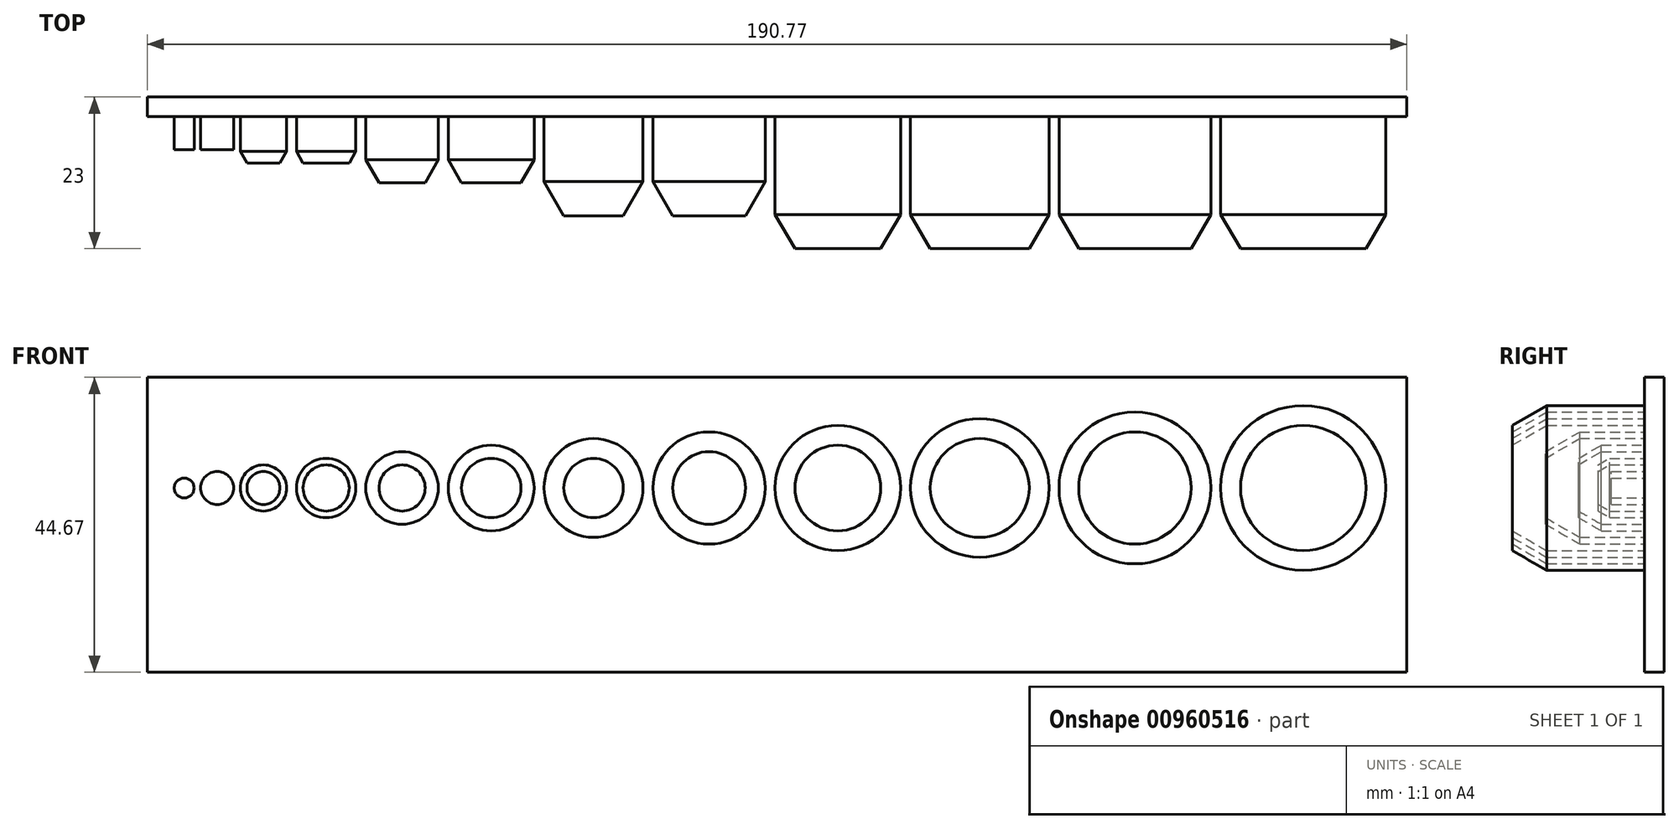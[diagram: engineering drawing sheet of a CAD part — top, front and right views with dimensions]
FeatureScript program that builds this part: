
annotation { "Feature Type Name" : "Feature", "Feature Type Description" : "" }
export const myFeature = defineFeature(function(context is Context, id is Id, definition is map)
    precondition{}
    {
        {
            var Q0;
            Q0=qCreatedBy(makeId("Front.planeOp"),FACE);
            var sketch = newSketch(context, id + "F0", { "sketchPlane" : qUnion([Q0])});
            skLineSegment(sketch, "E0", {"start": v(-30.94, 0) * mm, "end": v(30.94, 0) * mm, "construction": true});
            skCircle(sketch, "E1", {"center": v(-19.6, 0) * mm, "radius": 1.5 * mm});
            skCircle(sketch, "E2", {"center": v(-14.6, 0) * mm, "radius": 2.5 * mm});
            skCircle(sketch, "E3", {"center": v(-19.6, 0) * mm, "radius": 1.59 * mm});
            skCircle(sketch, "E4", {"center": v(-7.6, 0) * mm, "radius": 3.5 * mm});
            skCircle(sketch, "E5", {"center": v(1.9, 0) * mm, "radius": 4.5 * mm});
            skCircle(sketch, "E6", {"center": v(13.4, 0) * mm, "radius": 5.5 * mm});
            skCircle(sketch, "E7", {"center": v(26.9, 0) * mm, "radius": 6.5 * mm});
            skCircle(sketch, "E8", {"center": v(42.4, 0) * mm, "radius": 7.5 * mm});
            skCircle(sketch, "E9", {"center": v(59.9, 0) * mm, "radius": 8.5 * mm});
            skCircle(sketch, "E10", {"center": v(79.4, 0) * mm, "radius": 9.5 * mm});
            skLineSegment(sketch, "E11", {"start": v(50.7, 0) * mm, "end": v(122.59, 0) * mm, "construction": true});
            skCircle(sketch, "E12", {"center": v(100.9, 0) * mm, "radius": 10.5 * mm});
            skLineSegment(sketch, "E13", {"start": v(119.58, 0) * mm, "end": v(157.4, 0) * mm, "construction": true});
            skCircle(sketch, "E14", {"center": v(124.4, 0) * mm, "radius": 11.5 * mm});
            skCircle(sketch, "E15", {"center": v(149.9, 0) * mm, "radius": 12.5 * mm});
            skText(sketch, "E16", { "text": "25", "fontName": "OpenSans-Bold.ttf"});
            const initialGuessF0  = {"E16": [0.14266, -0.02711, 1, 0, 0.0101]};
            skSetInitialGuess(sketch, initialGuessF0);
            skSolve(sketch);
        }
        {
            var Q0;
            Q0=makeQuery(id+"F0.imprint","IMPRINT",FACE,{"disambiguationData":[TD([[makeQuery(id+"F0.imprint","IMPRINT",EDGE,{"derivedFrom":sQuery(id+"F0.wireOp",EDGE,"E1")}),1.0]])]});
            var Q1;
            Q1=makeQuery(id+"F0.imprint","IMPRINT",FACE,{"disambiguationData":[TD([[makeQuery(id+"F0.imprint","IMPRINT",EDGE,{"derivedFrom":sQuery(id+"F0.wireOp",EDGE,"E2")}),1.0]])]});
            extrude(context, id + "F1", {"entities" : qUnion([Q0, Q1]), "depth" : 5 * mm, "offsetDistance" : 25 * mm});
        }
        {
            var Q0;
            Q0=makeQuery(id+"F0.imprint","IMPRINT",FACE,{"disambiguationData":[TD([[makeQuery(id+"F0.imprint","IMPRINT",EDGE,{"derivedFrom":sQuery(id+"F0.wireOp",EDGE,"E4")}),1.0]])]});
            var Q1;
            Q1=makeQuery(id+"F0.imprint","IMPRINT",FACE,{"disambiguationData":[TD([[makeQuery(id+"F0.imprint","IMPRINT",EDGE,{"derivedFrom":sQuery(id+"F0.wireOp",EDGE,"E5")}),1.0]])]});
            extrude(context, id + "F2", {"entities" : qUnion([Q0, Q1]), "depth" : 7 * mm, "offsetDistance" : 25 * mm});
        }
        {
            var Q0;
            Q0=makeQuery(id+"F0.imprint","IMPRINT",FACE,{"disambiguationData":[TD([[makeQuery(id+"F0.imprint","IMPRINT",EDGE,{"derivedFrom":sQuery(id+"F0.wireOp",EDGE,"E6")}),1.0]])]});
            var Q1;
            Q1=makeQuery(id+"F0.imprint","IMPRINT",FACE,{"disambiguationData":[TD([[makeQuery(id+"F0.imprint","IMPRINT",EDGE,{"derivedFrom":sQuery(id+"F0.wireOp",EDGE,"E7")}),1.0]])]});
            extrude(context, id + "F3", {"entities" : qUnion([Q0, Q1]), "depth" : 10 * mm, "offsetDistance" : 25 * mm});
        }
        {
            var Q0;
            Q0=makeQuery(id+"F0.imprint","IMPRINT",FACE,{"disambiguationData":[TD([[makeQuery(id+"F0.imprint","IMPRINT",EDGE,{"derivedFrom":sQuery(id+"F0.wireOp",EDGE,"E8")}),1.0]])]});
            var Q1;
            Q1=makeQuery(id+"F0.imprint","IMPRINT",FACE,{"disambiguationData":[TD([[makeQuery(id+"F0.imprint","IMPRINT",EDGE,{"derivedFrom":sQuery(id+"F0.wireOp",EDGE,"E9")}),1.0]])]});
            extrude(context, id + "F4", {"entities" : qUnion([Q0, Q1]), "depth" : 15 * mm, "offsetDistance" : 25 * mm});
        }
        {
            var Q0;
            Q0=makeQuery(id+"F0.imprint","IMPRINT",FACE,{"disambiguationData":[TD([[makeQuery(id+"F0.imprint","IMPRINT",EDGE,{"derivedFrom":sQuery(id+"F0.wireOp",EDGE,"E10")}),1.0]])]});
            var Q1;
            Q1=makeQuery(id+"F0.imprint","IMPRINT",FACE,{"disambiguationData":[TD([[makeQuery(id+"F0.imprint","IMPRINT",EDGE,{"derivedFrom":sQuery(id+"F0.wireOp",EDGE,"E12")}),1.0]])]});
            extrude(context, id + "F5", {"entities" : qUnion([Q0, Q1]), "depth" : 20 * mm, "offsetDistance" : 25 * mm});
        }
        {
            var Q0;
            Q0=makeQuery(id+"F0.imprint","IMPRINT",FACE,{"disambiguationData":[TD([[makeQuery(id+"F0.imprint","IMPRINT",EDGE,{"derivedFrom":sQuery(id+"F0.wireOp",EDGE,"E14")}),1.0]])]});
            var Q1;
            Q1=makeQuery(id+"F0.imprint","IMPRINT",FACE,{"disambiguationData":[TD([[makeQuery(id+"F0.imprint","IMPRINT",EDGE,{"derivedFrom":sQuery(id+"F0.wireOp",EDGE,"E15")}),1.0]])]});
            extrude(context, id + "F6", {"entities" : qUnion([Q0, Q1]), "depth" : 20 * mm, "offsetDistance" : 25 * mm});
        }
        {
            var Q0;
            Q0=qCreatedBy(makeId("Front.planeOp"),FACE);
            var sketch = newSketch(context, id + "F7", { "sketchPlane" : qUnion([Q0])});
            skLineSegment(sketch, "E17.bottom", {"start": v(165.58, 16.76) * mm, "end": v(-25.2, 16.76) * mm});
            skLineSegment(sketch, "E17.top", {"start": v(165.58, -27.91) * mm, "end": v(-25.2, -27.91) * mm});
            skLineSegment(sketch, "E17.left", {"start": v(165.58, 16.76) * mm, "end": v(165.58, -27.91) * mm});
            skLineSegment(sketch, "E17.right", {"start": v(-25.2, 16.76) * mm, "end": v(-25.2, -27.91) * mm});
            skSolve(sketch);
        }
        {
            var Q0;
            Q0 = qSketchRegion(id + "F7", true);
            extrude(context, id + "F8", {"entities" : qUnion([Q0]), "oppositeDirection" : true, "depth" : 3 * mm, "offsetDistance" : 25 * mm});
        }
        {
            var Q0;
            Q0=makeQuery(id+"F6.opExtrude","CAP_EDGE",EDGE,{"disambiguationData":[OSD([sQuery(id+"F0.wireOp",EDGE,"E15")])],"isStart":false});
            var Q1;
            Q1=makeQuery(id+"F6.opExtrude","CAP_EDGE",EDGE,{"disambiguationData":[OSD([sQuery(id+"F0.wireOp",EDGE,"E14")])],"isStart":false});
            var Q2;
            Q2=makeQuery(id+"F5.opExtrude","CAP_EDGE",EDGE,{"disambiguationData":[OSD([sQuery(id+"F0.wireOp",EDGE,"E12")])],"isStart":false});
            var Q3;
            Q3=makeQuery(id+"F5.opExtrude","CAP_EDGE",EDGE,{"disambiguationData":[OSD([sQuery(id+"F0.wireOp",EDGE,"E10")])],"isStart":false});
            var Q4;
            Q4=makeQuery(id+"F4.opExtrude","CAP_EDGE",EDGE,{"disambiguationData":[OSD([sQuery(id+"F0.wireOp",EDGE,"E9")])],"isStart":false});
            var Q5;
            Q5=makeQuery(id+"F4.opExtrude","CAP_EDGE",EDGE,{"disambiguationData":[OSD([sQuery(id+"F0.wireOp",EDGE,"E8")])],"isStart":false});
            chamfer(context, id + "F9", {"entities" : qUnion([Q0, Q1, Q2, Q3, Q4, Q5]), "chamferType" : ChamferType.OFFSET_ANGLE, "width" : 3 * mm, "oppositeDirection" : false, "angle" : 60 * degree, "tangentPropagation" : true});
        }
        {
            var Q0;
            Q0=makeQuery(id+"F3.opExtrude","CAP_EDGE",EDGE,{"disambiguationData":[OSD([sQuery(id+"F0.wireOp",EDGE,"E7")])],"isStart":false});
            var Q1;
            Q1=makeQuery(id+"F3.opExtrude","CAP_EDGE",EDGE,{"disambiguationData":[OSD([sQuery(id+"F0.wireOp",EDGE,"E6")])],"isStart":false});
            chamfer(context, id + "F10", {"entities" : qUnion([Q0, Q1]), "chamferType" : ChamferType.OFFSET_ANGLE, "width" : 2 * mm, "oppositeDirection" : false, "angle" : 60 * degree, "tangentPropagation" : true});
        }
        {
            var Q0;
            Q0=makeQuery(id+"F2.opExtrude","CAP_EDGE",EDGE,{"disambiguationData":[OSD([sQuery(id+"F0.wireOp",EDGE,"E5")])],"isStart":false});
            var Q1;
            Q1=makeQuery(id+"F2.opExtrude","CAP_EDGE",EDGE,{"disambiguationData":[OSD([sQuery(id+"F0.wireOp",EDGE,"E4")])],"isStart":false});
            chamfer(context, id + "F11", {"entities" : qUnion([Q0, Q1]), "chamferType" : ChamferType.OFFSET_ANGLE, "width" : 1 * mm, "oppositeDirection" : false, "angle" : 60 * degree, "tangentPropagation" : true});
        }
    });
